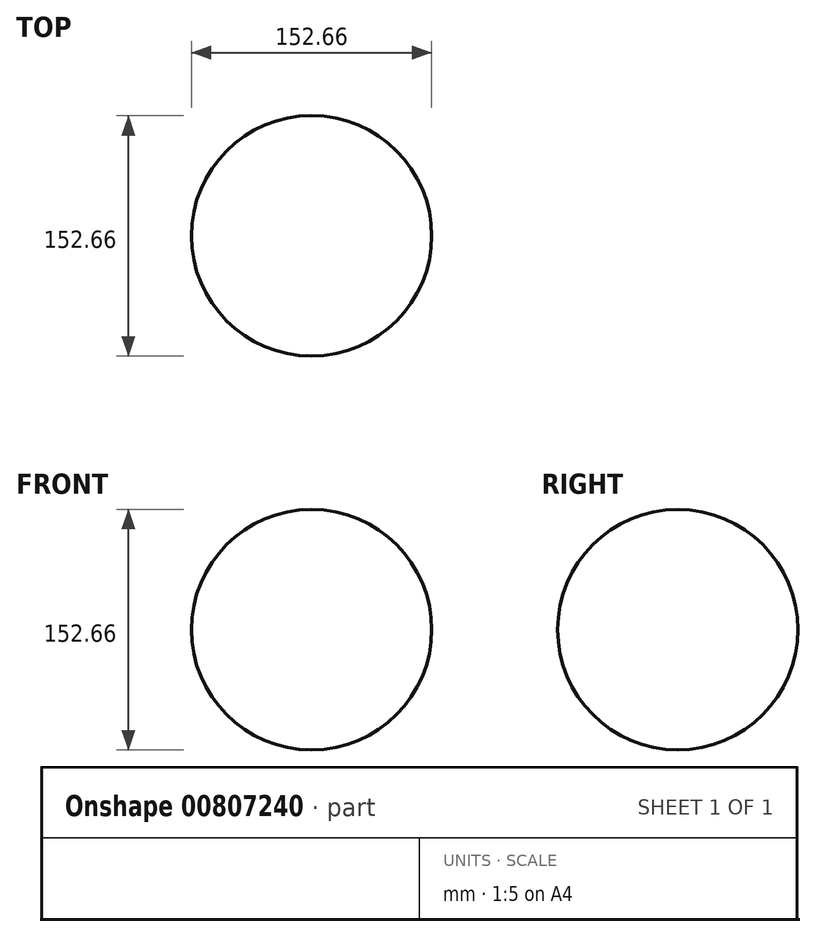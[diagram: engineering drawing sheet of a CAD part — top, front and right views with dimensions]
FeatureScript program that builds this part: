
annotation { "Feature Type Name" : "Feature", "Feature Type Description" : "" }
export const myFeature = defineFeature(function(context is Context, id is Id, definition is map)
    precondition{}
    {
        {
            var Q0;
            Q0=qCreatedBy(makeId("Front.planeOp"),FACE);
            var sketch = newSketch(context, id + "F0", { "sketchPlane" : qUnion([Q0])});
            skCircle(sketch, "E0", {"center": v(0, 0) * mm, "radius": 76.33 * mm});
            skLineSegment(sketch, "E1", {"start": v(0, 84.45) * mm, "end": v(0, -86.32) * mm});
            skSolve(sketch);
        }
        {
            var Q0;
            {var subQ0=sQuery(id+"F0.wireOp",EDGE,"E1");var subQ1=sQuery(id+"F0.wireOp",EDGE,"E0");var subQ2=makeQuery(id+"F0.imprint","INTERSECT",VERTEX,{"disambiguationData":[OD(0.0)],"derivedFrom":[subQ1,subQ0]});Q0=makeQuery(id+"F0.imprint","IMPRINT",FACE,{"disambiguationData":[TD([[makeQuery(id+"F0.imprint","IMPRINT",EDGE,{"disambiguationData":[TD([[subQ2,-1.0]])],"derivedFrom":subQ1}),1.0]])]});}
            var Q1;
            Q1=sQuery(id+"F0.wireOp",EDGE,"E1");
            revolve(context, id + "F1", {"surfaceOperationType" : NewSurfaceOperationType.NEW, "entities" : qUnion([Q0]), "axis" : qUnion([Q1]), "revolveType" : RevolveType.FULL});
        }
    });
